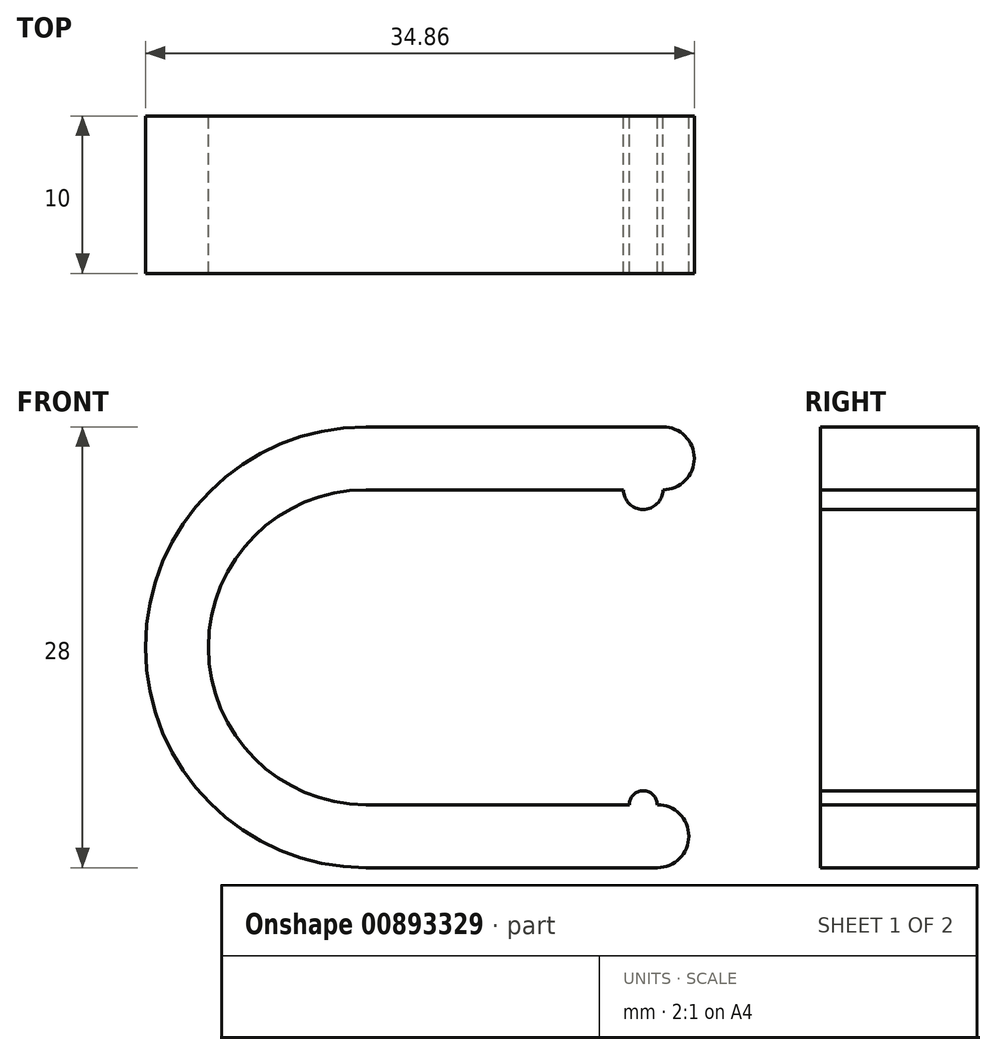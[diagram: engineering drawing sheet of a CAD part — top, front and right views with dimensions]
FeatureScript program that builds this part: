
annotation { "Feature Type Name" : "Feature", "Feature Type Description" : "" }
export const myFeature = defineFeature(function(context is Context, id is Id, definition is map)
    precondition{}
    {
        {
            var Q0;
            Q0=qCreatedBy(makeId("Front.planeOp"),FACE);
            var sketch = newSketch(context, id + "F0", { "sketchPlane" : qUnion([Q0])});
            skArc(sketch, "E0", {"start": v(0, 10) * mm, "mid": v(-10, 0) * mm, "end": v(0, -10) * mm});
            skLineSegment(sketch, "E1", {"start": v(0, 10) * mm, "end": v(18.86, 10) * mm});
            skLineSegment(sketch, "E2", {"start": v(0, -10) * mm, "end": v(18.5, -10) * mm});
            skLineSegment(sketch, "E3", {"start": v(18.5, -10) * mm, "end": v(18.5, -14) * mm});
            skArc(sketch, "E4", {"start": v(0, 14) * mm, "mid": v(-14, 0) * mm, "end": v(0, -14) * mm});
            skLineSegment(sketch, "E5", {"start": v(18.86, 10) * mm, "end": v(18.86, 14) * mm});
            skLineSegment(sketch, "E6", {"start": v(18.86, 14) * mm, "end": v(0, 14) * mm});
            skLineSegment(sketch, "E7", {"start": v(18.5, -14) * mm, "end": v(0, -14) * mm});
            skArc(sketch, "E8", {"start": v(18.5, -14) * mm, "mid": v(20.5, -12) * mm, "end": v(18.5, -10) * mm});
            skArc(sketch, "E9", {"start": v(18.86, 10) * mm, "mid": v(20.86, 12) * mm, "end": v(18.86, 14) * mm});
            skArc(sketch, "E10", {"start": v(16.36, 10) * mm, "mid": v(17.6, 8.75) * mm, "end": v(18.86, 10) * mm});
            skArc(sketch, "E11", {"start": v(18.5, -10) * mm, "mid": v(17.62, -9.11) * mm, "end": v(16.73, -10) * mm});
            skSolve(sketch);
        }
        {
            var Q0;
            {var subQ1=sQuery(id+"F0.wireOp",EDGE,"E0");Q0=makeQuery(id+"F0.imprint","IMPRINT",FACE,{"disambiguationData":[TD([[makeQuery(id+"F0.imprint","IMPRINT",EDGE,{"derivedFrom":subQ1}),-1.0]])]});}
            var Q1;
            Q1=makeQuery(id+"F0.imprint","IMPRINT",FACE,{"disambiguationData":[TD([[makeQuery(id+"F0.imprint","IMPRINT",EDGE,{"derivedFrom":sQuery(id+"F0.wireOp",EDGE,"E5")}),-1.0]])]});
            var Q2;
            {var subQ0=sQuery(id+"F0.wireOp",EDGE,"E10");Q2=makeQuery(id+"F0.imprint","IMPRINT",FACE,{"disambiguationData":[TD([[makeQuery(id+"F0.imprint","IMPRINT",EDGE,{"derivedFrom":subQ0}),1.0]])]});}
            var Q3;
            Q3=makeQuery(id+"F0.imprint","IMPRINT",FACE,{"disambiguationData":[TD([[makeQuery(id+"F0.imprint","IMPRINT",EDGE,{"derivedFrom":sQuery(id+"F0.wireOp",EDGE,"E3")}),1.0]])]});
            var Q4;
            {var subQ0=sQuery(id+"F0.wireOp",EDGE,"E11");Q4=makeQuery(id+"F0.imprint","IMPRINT",FACE,{"disambiguationData":[TD([[makeQuery(id+"F0.imprint","IMPRINT",EDGE,{"derivedFrom":subQ0}),1.0]])]});}
            extrude(context, id + "F1", {"entities" : qUnion([Q0, Q1, Q2, Q3, Q4]), "depth" : 10 * mm, "offsetDistance" : 25 * mm});
        }
    });
